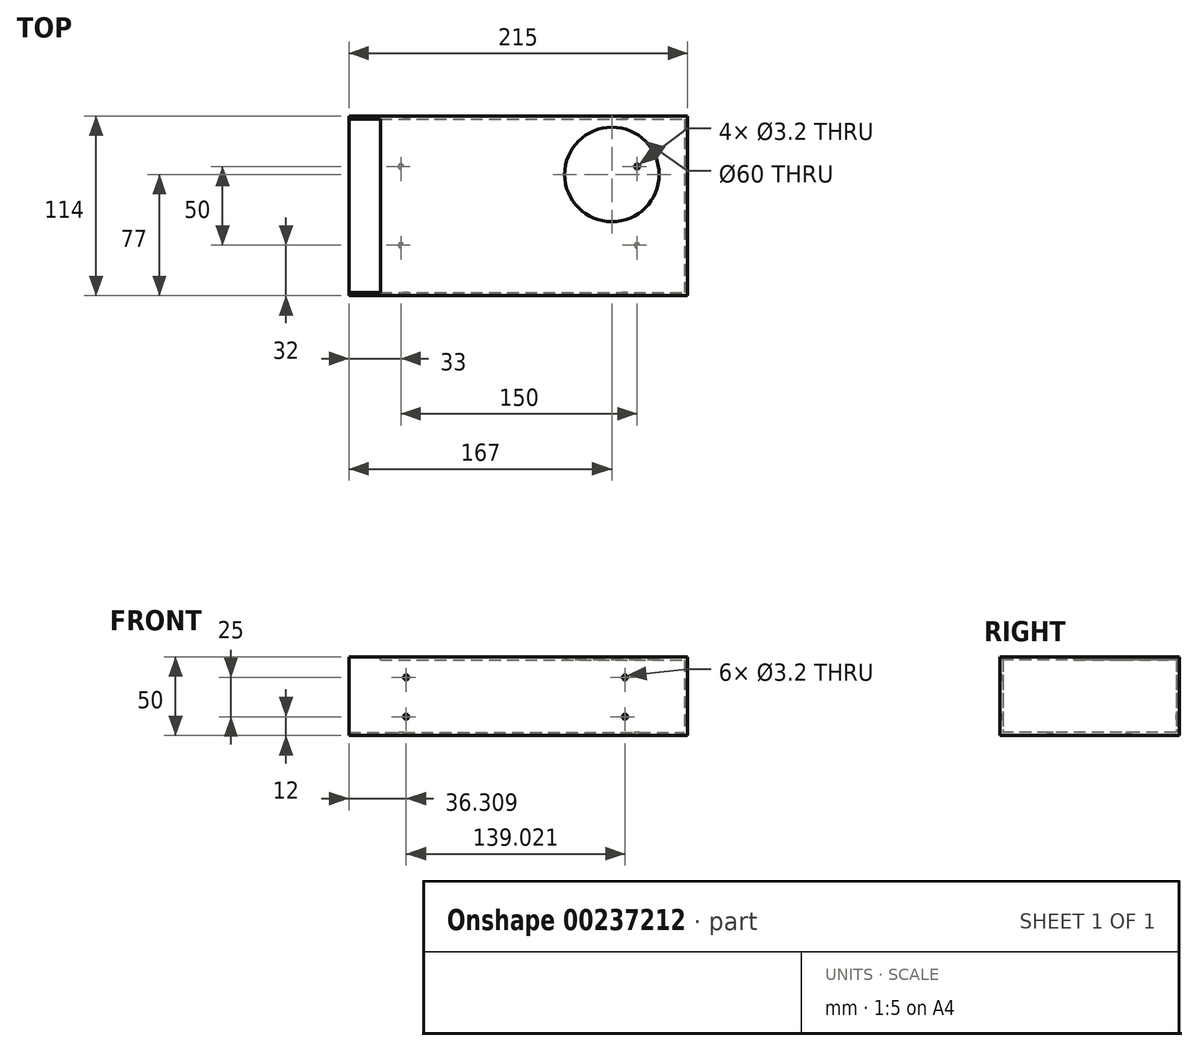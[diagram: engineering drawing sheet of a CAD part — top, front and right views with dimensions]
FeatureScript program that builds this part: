
annotation { "Feature Type Name" : "Feature", "Feature Type Description" : "" }
export const myFeature = defineFeature(function(context is Context, id is Id, definition is map)
    precondition{}
    {
        {
            var Q0;
            Q0=qCreatedBy(makeId("Top.planeOp"),FACE);
            var sketch = newSketch(context, id + "F0", { "sketchPlane" : qUnion([Q0])});
            skLineSegment(sketch, "E0.bottom", {"start": v(-107.5, 57) * mm, "end": v(107.5, 57) * mm});
            skLineSegment(sketch, "E0.top", {"start": v(-107.5, -57) * mm, "end": v(107.5, -57) * mm});
            skLineSegment(sketch, "E0.left", {"start": v(-107.5, 57) * mm, "end": v(-107.5, -57) * mm});
            skLineSegment(sketch, "E0.right", {"start": v(107.5, 57) * mm, "end": v(107.5, -57) * mm});
            skPoint(sketch, "E1", {"position": v(107.5, 0) * mm});
            skPoint(sketch, "E2", {"position": v(0, -57) * mm});
            skSolve(sketch);
        }
        {
            var Q0;
            Q0=makeQuery(id+"F0.imprint","IMPRINT",FACE,{"disambiguationData":[TD([[makeQuery(id+"F0.imprint","IMPRINT",EDGE,{"derivedFrom":sQuery(id+"F0.wireOp",EDGE,"E0.bottom")}),-1.0]])]});
            extrude(context, id + "F1", {"entities" : qUnion([Q0]), "depth" : 50 * mm});
        }
        {
            var Q0;
            Q0=makeQuery(id+"F1.opExtrude","SWEPT_FACE",FACE,{"disambiguationData":[OSD([sQuery(id+"F0.wireOp",EDGE,"E0.left")])]});
            shell(context, id + "F2", {"entities" : qUnion([Q0]), "thickness" : 2 * mm});
        }
        {
            var Q0;
            Q0=makeQuery(id+"F1.opExtrude","CAP_FACE",FACE,{"disambiguationData":[OSD([sQuery(id+"F0.wireOp",EDGE,"E0.bottom"),sQuery(id+"F0.wireOp",EDGE,"E0.top"),sQuery(id+"F0.wireOp",EDGE,"E0.left"),sQuery(id+"F0.wireOp",EDGE,"E0.right")])],"isStart":false});
            var sketch = newSketch(context, id + "F3", { "sketchPlane" : qUnion([Q0])});
            skCircle(sketch, "E3", {"center": v(59.5, 20) * mm, "radius": 30 * mm});
            skLineSegment(sketch, "E4.bottom", {"start": v(-107.5, 55) * mm, "end": v(-87.5, 55) * mm});
            skLineSegment(sketch, "E4.top", {"start": v(-107.5, -55) * mm, "end": v(-87.5, -55) * mm});
            skLineSegment(sketch, "E4.left", {"start": v(-107.5, 55) * mm, "end": v(-107.5, -55) * mm});
            skLineSegment(sketch, "E4.right", {"start": v(-87.5, 55) * mm, "end": v(-87.5, -55) * mm});
            skSolve(sketch);
        }
        {
            var Q0;
            Q0=makeQuery(id+"F3.imprint","IMPRINT",FACE,{"disambiguationData":[TD([[makeQuery(id+"F3.imprint","IMPRINT",EDGE,{"derivedFrom":sQuery(id+"F3.wireOp",EDGE,"E4.bottom")}),-1.0]])]});
            var Q1;
            Q1=makeQuery(id+"F3.imprint","IMPRINT",FACE,{"disambiguationData":[TD([[makeQuery(id+"F3.imprint","IMPRINT",EDGE,{"derivedFrom":sQuery(id+"F3.wireOp",EDGE,"E3")}),1.0]])]});
            extrude(context, id + "F4", {"entities" : qUnion([Q0, Q1]), "operationType" : NewBodyOperationType.REMOVE, "endBound" : BoundingType.UP_TO_NEXT, "oppositeDirection" : true, "depth" : 25 * mm});
        }
        {
            var Q0;
            Q0=makeQuery(id+"F1.opExtrude","SWEPT_FACE",FACE,{"disambiguationData":[OSD([sQuery(id+"F0.wireOp",EDGE,"E0.top")])]});
            var sketch = newSketch(context, id + "F5", { "sketchPlane" : qUnion([Q0])});
            skPoint(sketch, "E5", {"position": v(-71.2, 37) * mm});
            skPoint(sketch, "E6", {"position": v(-71.2, 12) * mm});
            skPoint(sketch, "E7", {"position": v(67.83, 37) * mm});
            skPoint(sketch, "E8", {"position": v(67.83, 12) * mm});
            skSolve(sketch);
        }
        {
            var Q0;
            Q0=makeQuery(id+"F1.opExtrude","SWEPT_FACE",FACE,{"disambiguationData":[OSD([sQuery(id+"F0.wireOp",EDGE,"E0.bottom")])]});
            var sketch = newSketch(context, id + "F6", { "sketchPlane" : qUnion([Q0])});
            skPoint(sketch, "E9", {"position": v(-67.83, 12) * mm});
            skPoint(sketch, "E10", {"position": v(71.2, 12) * mm});
            skSolve(sketch);
        }
        {
            var Q0;
            Q0=makeQuery(id+"F1.opExtrude","CAP_FACE",FACE,{"disambiguationData":[OSD([sQuery(id+"F0.wireOp",EDGE,"E0.bottom"),sQuery(id+"F0.wireOp",EDGE,"E0.top"),sQuery(id+"F0.wireOp",EDGE,"E0.left"),sQuery(id+"F0.wireOp",EDGE,"E0.right")])],"isStart":true});
            var sketch = newSketch(context, id + "F7", { "sketchPlane" : qUnion([Q0])});
            skPoint(sketch, "E11", {"position": v(-74.5, 25) * mm});
            skPoint(sketch, "E12", {"position": v(75.5, 25) * mm});
            skPoint(sketch, "E13", {"position": v(75.5, -25) * mm});
            skPoint(sketch, "E14", {"position": v(-74.5, -25) * mm});
            skSolve(sketch);
        }
        {
            var Q0;
            Q0=sQuery(id+"F7.wireOp",VERTEX,"E11");
            var Q1;
            Q1=sQuery(id+"F7.wireOp",VERTEX,"E14");
            var Q2;
            Q2=sQuery(id+"F7.wireOp",VERTEX,"E13");
            var Q3;
            Q3=sQuery(id+"F7.wireOp",VERTEX,"E12");
            var Q4;
            Q4=sQuery(id+"F5.wireOp",VERTEX,"E5");
            var Q5;
            Q5=sQuery(id+"F5.wireOp",VERTEX,"E6");
            var Q6;
            Q6=sQuery(id+"F5.wireOp",VERTEX,"E7");
            var Q7;
            Q7=sQuery(id+"F5.wireOp",VERTEX,"E8");
            var Q8;
            Q8=sQuery(id+"F6.wireOp",VERTEX,"E10");
            var Q9;
            Q9=sQuery(id+"F6.wireOp",VERTEX,"E9");
            var Q10;
            Q10=makeQuery(id+"F1.opExtrude","SWEPT_BODY",BODY,{"disambiguationData":[OSD([sQuery(id+"F0.wireOp",EDGE,"E0.bottom"),sQuery(id+"F0.wireOp",EDGE,"E0.top"),sQuery(id+"F0.wireOp",EDGE,"E0.left"),sQuery(id+"F0.wireOp",EDGE,"E0.right")])]});
            hole(context, id + "F8", {"style" : HoleStyle.SIMPLE, "endStyle" : HoleEndStyle.BLIND, "standardTappedOrClearance" : lookupTablePath({ "standard" : "ISO", "engagement" : "75%", "pitch" : "0.75 mm", "size" : "M4", "type" : "Tapped" }), "standardBlindInLast" : lookupTablePath({ "standard" : "ISO", "engagement" : "75%", "pitch" : "0.75 mm", "size" : "M4", "type" : "Tapped" }), "holeDiameter" : 3.2 * mm, "holeDepth" : 2 * mm, "startFromSketch" : true, "locations" : qUnion([Q0, Q1, Q2, Q3, Q4, Q5, Q6, Q7, Q8, Q9]), "scope" : qUnion([Q10])});
        }
    });
